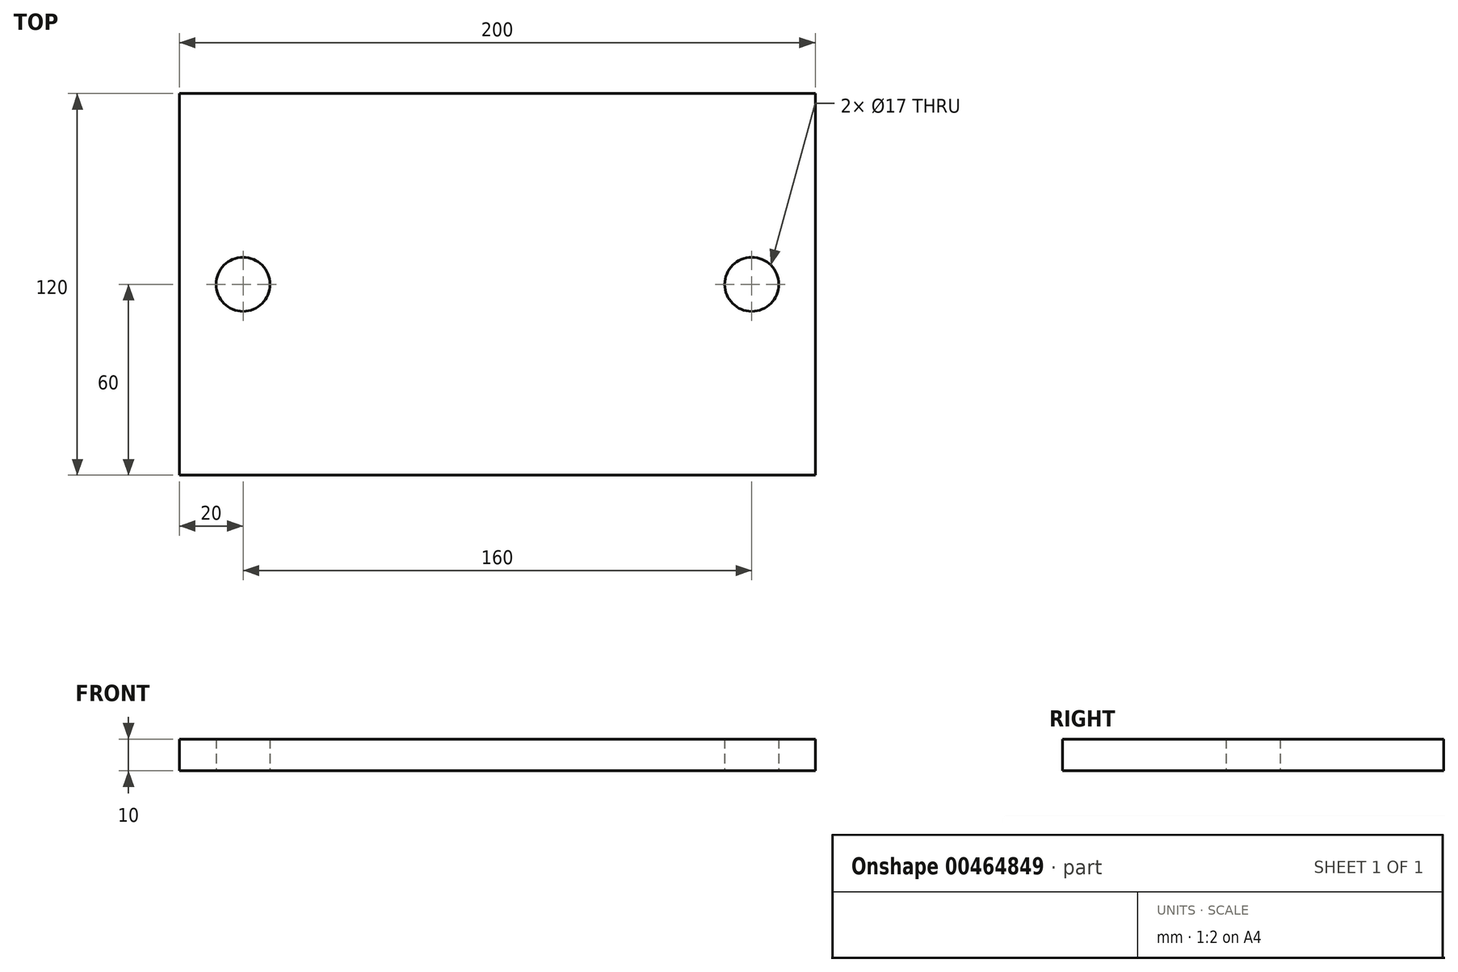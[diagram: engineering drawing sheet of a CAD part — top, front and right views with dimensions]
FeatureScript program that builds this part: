
annotation { "Feature Type Name" : "Feature", "Feature Type Description" : "" }
export const myFeature = defineFeature(function(context is Context, id is Id, definition is map)
    precondition{}
    {
        {
            var Q0;
            Q0=qCreatedBy(makeId("Top.planeOp"),FACE);
            var sketch = newSketch(context, id + "F0", { "sketchPlane" : qUnion([Q0])});
            skLineSegment(sketch, "E0.bottom", {"start": v(-100, 60) * mm, "end": v(100, 60) * mm});
            skLineSegment(sketch, "E0.top", {"start": v(-100, -60) * mm, "end": v(100, -60) * mm});
            skLineSegment(sketch, "E0.left", {"start": v(-100, 60) * mm, "end": v(-100, -60) * mm});
            skLineSegment(sketch, "E0.right", {"start": v(100, 60) * mm, "end": v(100, -60) * mm});
            skCircle(sketch, "E1", {"center": v(-80, 0) * mm, "radius": 8.5 * mm});
            skCircle(sketch, "E2", {"center": v(80, 0) * mm, "radius": 8.5 * mm});
            skSolve(sketch);
        }
        {
            var Q0;
            Q0=makeQuery(id+"F0.imprint","IMPRINT",FACE,{"disambiguationData":[TD([[makeQuery(id+"F0.imprint","IMPRINT",EDGE,{"derivedFrom":sQuery(id+"F0.wireOp",EDGE,"E0.bottom")}),-1.0]])]});
            extrude(context, id + "F1", {"entities" : qUnion([Q0]), "depth" : 10 * mm});
        }
    });
